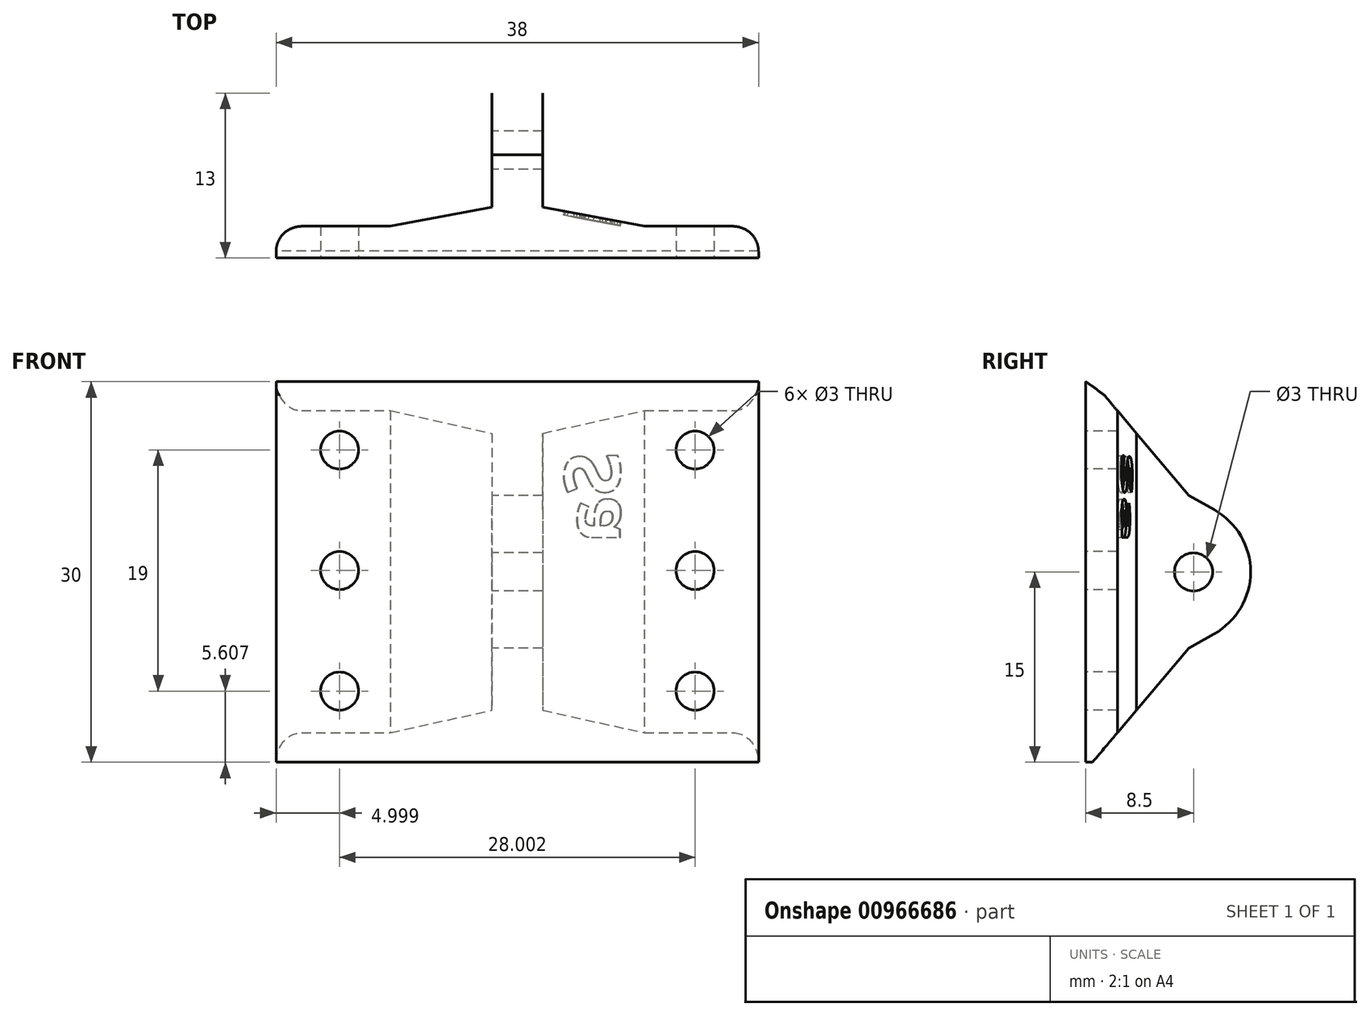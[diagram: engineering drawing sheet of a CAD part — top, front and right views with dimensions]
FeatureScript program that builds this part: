
annotation { "Feature Type Name" : "Feature", "Feature Type Description" : "" }
export const myFeature = defineFeature(function(context is Context, id is Id, definition is map)
    precondition{}
    {
        {
            var Q0;
            Q0=qCreatedBy(makeId("Top.planeOp"),FACE);
            var sketch = newSketch(context, id + "F0", { "sketchPlane" : qUnion([Q0])});
            skLineSegment(sketch, "E0", {"start": v(0, 0) * mm, "end": v(38, 0) * mm});
            skLineSegment(sketch, "E1", {"start": v(38, 0) * mm, "end": v(38, 2.5) * mm});
            skLineSegment(sketch, "E2", {"start": v(21, 4) * mm, "end": v(21, 13) * mm});
            skLineSegment(sketch, "E3", {"start": v(21, 13) * mm, "end": v(17, 13) * mm});
            skLineSegment(sketch, "E4", {"start": v(0, 2.5) * mm, "end": v(0, 0) * mm});
            skLineSegment(sketch, "E5", {"start": v(17, 13) * mm, "end": v(17, 4) * mm});
            skLineSegment(sketch, "E6", {"start": v(17, 4) * mm, "end": v(9, 2.5) * mm});
            skLineSegment(sketch, "E7", {"start": v(9, 2.5) * mm, "end": v(0, 2.5) * mm});
            skLineSegment(sketch, "E8", {"start": v(38, 2.5) * mm, "end": v(29, 2.5) * mm});
            skLineSegment(sketch, "E9", {"start": v(29, 2.5) * mm, "end": v(21, 4) * mm});
            skLineSegment(sketch, "E10", {"start": v(17, 4) * mm, "end": v(21, 4) * mm});
            skSolve(sketch);
        }
        {
            var Q0;
            Q0=qSketchRegion(id+"F0",true);
            var Q1;
            Q1=qSketchRegion(id+"F2",true);
            extrude(context, id + "F1", {"entities" : qUnion([Q0, Q1]), "depth" : 30 * mm, "offsetDistance" : 25 * mm});
        }
        {
            var Q0;
            Q0=qCreatedBy(makeId("Right.planeOp"),FACE);
            var sketch = newSketch(context, id + "F2", { "sketchPlane" : qUnion([Q0])});
            skLineSegment(sketch, "E11", {"start": v(14, 17.73) * mm, "end": v(8.13, 21.02) * mm});
            skLineSegment(sketch, "E12", {"start": v(8.13, 21.02) * mm, "end": v(0.55, 30.03) * mm});
            skLineSegment(sketch, "E13", {"start": v(14, 12.28) * mm, "end": v(8.13, 9) * mm});
            skLineSegment(sketch, "E14", {"start": v(8.13, 9) * mm, "end": v(0.55, 0) * mm});
            skLineSegment(sketch, "E15", {"start": v(0.55, 0) * mm, "end": v(14, 0) * mm});
            skLineSegment(sketch, "E16", {"start": v(14, 0) * mm, "end": v(14, 12.28) * mm});
            skLineSegment(sketch, "E17", {"start": v(14, 17.73) * mm, "end": v(14, 30) * mm});
            skLineSegment(sketch, "E18", {"start": v(14, 30) * mm, "end": v(0.55, 30.03) * mm});
            skSolve(sketch);
        }
        {
            var Q0;
            Q0=makeQuery(id+"F1.opExtrude","SWEPT_FACE",FACE,{"disambiguationData":[OSD([sQuery(id+"F0.wireOp",EDGE,"E5")])]});
            var sketch = newSketch(context, id + "F3", { "sketchPlane" : qUnion([Q0])});
            skPoint(sketch, "E19", {"position": v(-8.5, 15) * mm});
            skPoint(sketch, "E19.positionSnap0", {"position": v(-8.5, 0) * mm});
            skPoint(sketch, "E19.positionSnap1", {"position": v(-4, 15) * mm});
            skSolve(sketch);
        }
        {
            var Q0;
            Q0=qSketchRegion(id+"F2",true);
            extrude(context, id + "F4", {"entities" : qUnion([Q0]), "operationType" : NewBodyOperationType.REMOVE, "depth" : 39 * mm, "offsetDistance" : 25 * mm});
        }
        {
            var Q0;
            Q0=sQuery(id+"F3.wireOp",VERTEX,"E19");
            var Q1;
            Q1=makeQuery(id+"F1.opExtrude","SWEPT_BODY",BODY,{"disambiguationData":[OSD([sQuery(id+"F0.wireOp",EDGE,"E0"),sQuery(id+"F0.wireOp",EDGE,"E1"),sQuery(id+"F0.wireOp",EDGE,"E2"),sQuery(id+"F0.wireOp",EDGE,"E3"),sQuery(id+"F0.wireOp",EDGE,"E4"),sQuery(id+"F0.wireOp",EDGE,"E5"),sQuery(id+"F0.wireOp",EDGE,"E6"),sQuery(id+"F0.wireOp",EDGE,"E7"),sQuery(id+"F0.wireOp",EDGE,"E8"),sQuery(id+"F0.wireOp",EDGE,"E9")])]});
            hole(context, id + "F5", {"style" : HoleStyle.SIMPLE, "endStyle" : HoleEndStyle.THROUGH, "holeDiameter" : 3 * mm, "majorDiameter" : 5 * mm, "isTappedThrough" : true, "tappedDepth" : 12 * mm, "tapClearance" : 3, "locations" : qUnion([Q0]), "scope" : qUnion([Q1])});
        }
        {
            var Q0;
            Q0=makeQuery(id+"F4.boolean.opBoolean","COPY",EDGE,{"derivedFrom":makeQuery(id+"F4.opExtrude","SWEPT_EDGE",EDGE,{"disambiguationData":[OSD([sQuery(id+"F2.wireOp",EDGE,"E14"),sQuery(id+"F2.wireOp",EDGE,"E15")])]})});
            var Q1;
            Q1=makeQuery(id+"F4.boolean.opBoolean","INTERSECT",EDGE,{"derivedFrom":[makeQuery(id+"F1.opExtrude","CAP_FACE",FACE,{"disambiguationData":[OSD([sQuery(id+"F0.wireOp",EDGE,"E0"),sQuery(id+"F0.wireOp",EDGE,"E1"),sQuery(id+"F0.wireOp",EDGE,"E2"),sQuery(id+"F0.wireOp",EDGE,"E3"),sQuery(id+"F0.wireOp",EDGE,"E4"),sQuery(id+"F0.wireOp",EDGE,"E5"),sQuery(id+"F0.wireOp",EDGE,"E6"),sQuery(id+"F0.wireOp",EDGE,"E7"),sQuery(id+"F0.wireOp",EDGE,"E8"),sQuery(id+"F0.wireOp",EDGE,"E9")])],"isStart":false}),makeQuery(id+"F4.opExtrude","SWEPT_FACE",FACE,{"disambiguationData":[OSD([sQuery(id+"F2.wireOp",EDGE,"E12")])]})]});
            fillet(context, id + "F6", {"entities" : qUnion([Q0, Q1]), "radius" : 4 * mm, "tangentPropagation" : true, "rho" : 0.1, "crossSection" : FilletCrossSection.CONIC, "allowEdgeOverflow" : false});
        }
        {
            var Q0;
            Q0=makeQuery(id+"F1.opExtrude","SWEPT_EDGE",EDGE,{"disambiguationData":[OSD([sQuery(id+"F0.wireOp",EDGE,"E4"),sQuery(id+"F0.wireOp",EDGE,"E7")])]});
            var Q1;
            Q1=makeQuery(id+"F1.opExtrude","SWEPT_EDGE",EDGE,{"disambiguationData":[OSD([sQuery(id+"F0.wireOp",EDGE,"E1"),sQuery(id+"F0.wireOp",EDGE,"E8")])]});
            fillet(context, id + "F7", {"entities" : qUnion([Q0, Q1]), "radius" : 2 * mm, "tangentPropagation" : true, "allowEdgeOverflow" : false});
        }
        {
            var Q0;
            Q0=qCreatedBy(makeId("Front.planeOp"),FACE);
            var sketch = newSketch(context, id + "F8", { "sketchPlane" : qUnion([Q0])});
            skPoint(sketch, "E20", {"position": v(33, 24.6) * mm});
            skPoint(sketch, "E21", {"position": v(33, 15.1) * mm});
            skPoint(sketch, "E22", {"position": v(33, 5.6) * mm});
            skPoint(sketch, "E23", {"position": v(5, 5.6) * mm});
            skPoint(sketch, "E24", {"position": v(5, 15.1) * mm});
            skPoint(sketch, "E25", {"position": v(5, 24.6) * mm});
            skSolve(sketch);
        }
        {
            var Q0;
            Q0=sQuery(id+"F8.wireOp",VERTEX,"E20");
            var Q1;
            Q1=sQuery(id+"F8.wireOp",VERTEX,"E21");
            var Q2;
            Q2=sQuery(id+"F8.wireOp",VERTEX,"E22");
            var Q3;
            Q3=sQuery(id+"F8.wireOp",VERTEX,"E25");
            var Q4;
            Q4=sQuery(id+"F8.wireOp",VERTEX,"E24");
            var Q5;
            Q5=sQuery(id+"F8.wireOp",VERTEX,"E23");
            var Q6;
            Q6=makeQuery(id+"F1.opExtrude","SWEPT_BODY",BODY,{"disambiguationData":[OSD([sQuery(id+"F0.wireOp",EDGE,"E0"),sQuery(id+"F0.wireOp",EDGE,"E1"),sQuery(id+"F0.wireOp",EDGE,"E2"),sQuery(id+"F0.wireOp",EDGE,"E3"),sQuery(id+"F0.wireOp",EDGE,"E4"),sQuery(id+"F0.wireOp",EDGE,"E5"),sQuery(id+"F0.wireOp",EDGE,"E6"),sQuery(id+"F0.wireOp",EDGE,"E7"),sQuery(id+"F0.wireOp",EDGE,"E8"),sQuery(id+"F0.wireOp",EDGE,"E9")])]});
            hole(context, id + "F9", {"style" : HoleStyle.SIMPLE, "endStyle" : HoleEndStyle.THROUGH, "holeDiameter" : 3 * mm, "majorDiameter" : 5 * mm, "isTappedThrough" : true, "tappedDepth" : 12 * mm, "tapClearance" : 3, "locations" : qUnion([Q0, Q1, Q2, Q3, Q4, Q5]), "scope" : qUnion([Q6])});
        }
        {
            var Q0;
            Q0=makeQuery(id+"F1.opExtrude","SWEPT_FACE",FACE,{"disambiguationData":[OSD([sQuery(id+"F0.wireOp",EDGE,"E9")])]});
            var sketch = newSketch(context, id + "F10", { "sketchPlane" : qUnion([Q0])});
            skText(sketch, "E26", { "text": "Sa", "fontName": "OpenSans-Bold.ttf"});
            const initialGuessF10  = {"E26": [-0.02614, 0.02444, 0, -1, 0.00448]};
            skSetInitialGuess(sketch, initialGuessF10);
            skSolve(sketch);
        }
        {
            var Q0;
            Q0=qSketchRegion(id+"F10",true);
            extrude(context, id + "F11", {"entities" : qUnion([Q0]), "operationType" : NewBodyOperationType.REMOVE, "oppositeDirection" : true, "depth" : 0.3 * mm, "offsetDistance" : 25 * mm});
        }
        {
            var Q0;
            Q0=makeQuery(id+"F4.boolean.opBoolean","INTERSECT",EDGE,{"derivedFrom":[makeQuery(id+"F1.opExtrude","SWEPT_FACE",FACE,{"disambiguationData":[OSD([sQuery(id+"F0.wireOp",EDGE,"E3")])]}),makeQuery(id+"F4.opExtrude","SWEPT_FACE",FACE,{"disambiguationData":[OSD([sQuery(id+"F2.wireOp",EDGE,"E11")])]})]});
            var Q1;
            Q1=makeQuery(id+"F4.boolean.opBoolean","INTERSECT",EDGE,{"derivedFrom":[makeQuery(id+"F1.opExtrude","SWEPT_FACE",FACE,{"disambiguationData":[OSD([sQuery(id+"F0.wireOp",EDGE,"E3")])]}),makeQuery(id+"F4.opExtrude","SWEPT_FACE",FACE,{"disambiguationData":[OSD([sQuery(id+"F2.wireOp",EDGE,"E13")])]})]});
            fillet(context, id + "F12", {"entities" : qUnion([Q0, Q1]), "radius" : 5.63 * mm, "tangentPropagation" : true, "allowEdgeOverflow" : false});
        }
    });
